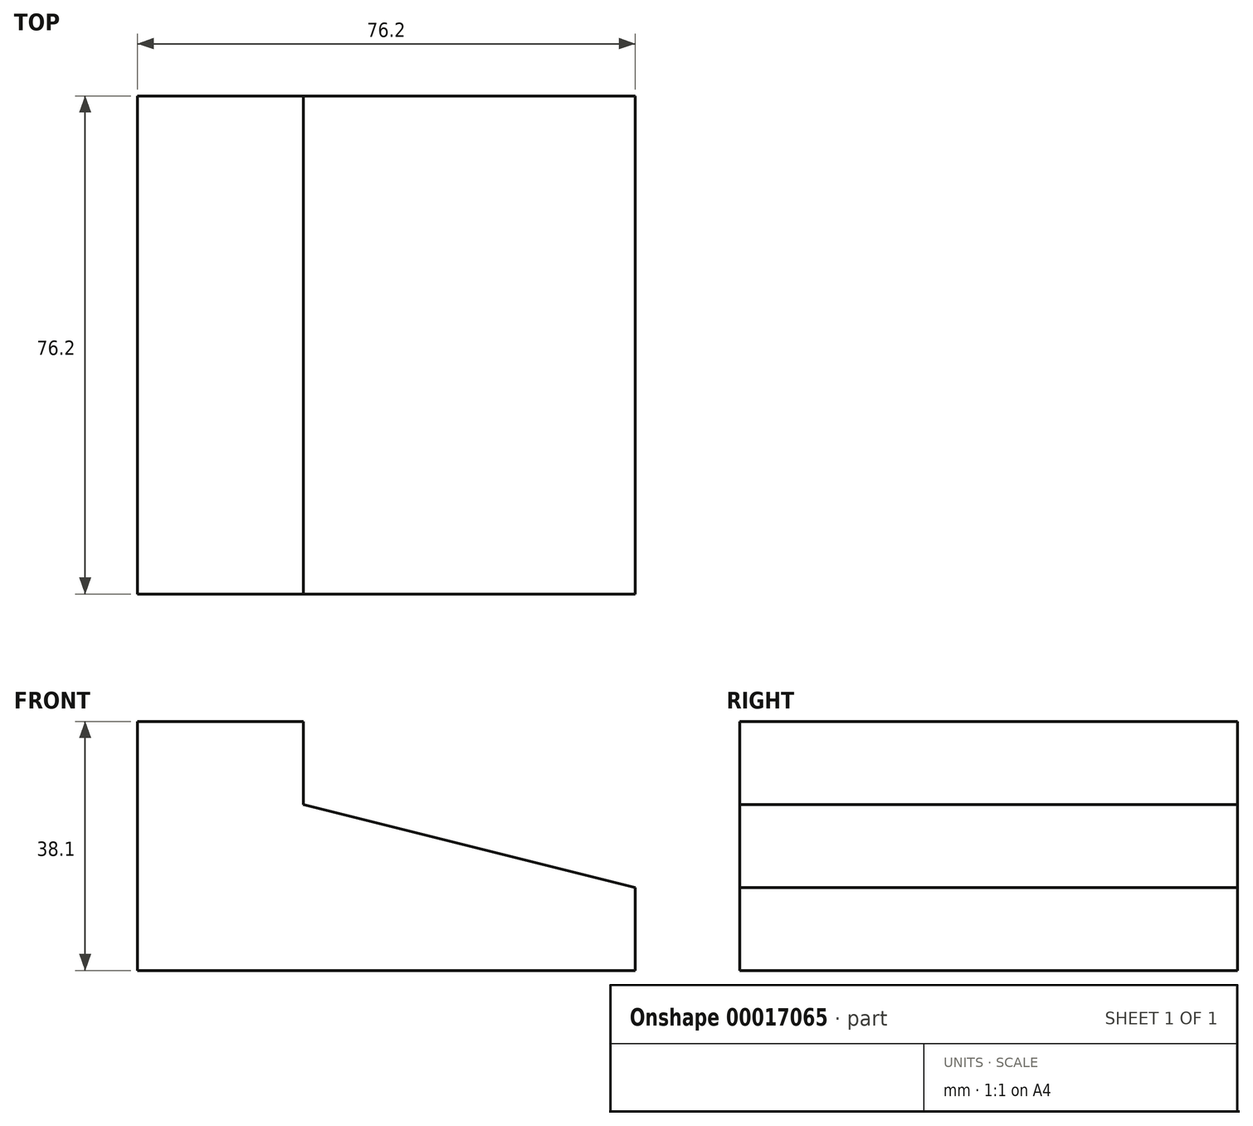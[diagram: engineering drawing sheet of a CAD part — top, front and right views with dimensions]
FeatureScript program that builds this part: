
annotation { "Feature Type Name" : "Feature", "Feature Type Description" : "" }
export const myFeature = defineFeature(function(context is Context, id is Id, definition is map)
    precondition{}
    {
        {
            var Q0;
            Q0=qCreatedBy(makeId("Front.planeOp"),FACE);
            var sketch = newSketch(context, id + "F0", { "sketchPlane" : qUnion([Q0])});
            skLineSegment(sketch, "E0", {"start": v(-49.4, 14.3) * mm, "end": v(-49.4, -23.8) * mm});
            skLineSegment(sketch, "E1", {"start": v(-49.4, -23.8) * mm, "end": v(26.8, -23.8) * mm});
            skLineSegment(sketch, "E2", {"start": v(-49.4, 14.3) * mm, "end": v(-24, 14.3) * mm});
            skLineSegment(sketch, "E3", {"start": v(-24, 14.3) * mm, "end": v(-24, 1.6) * mm});
            skLineSegment(sketch, "E4", {"start": v(-24, 1.6) * mm, "end": v(26.8, -11.1) * mm});
            skLineSegment(sketch, "E5", {"start": v(26.8, -11.1) * mm, "end": v(26.8, -23.8) * mm});
            skSolve(sketch);
        }
        {
            var Q0;
            Q0 = qSketchRegion(id + "F0", true);
            extrude(context, id + "F1", {"entities" : qUnion([Q0]), "depth" : 76.2 * mm});
        }
    });
